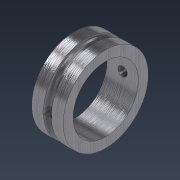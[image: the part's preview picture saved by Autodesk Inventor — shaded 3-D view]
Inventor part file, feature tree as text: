
AUTODESK INVENTOR PART (.ipt)
format: ipt  version: 2022 (Build 260153000, 153)  size: 160,256 bytes
history: native  units: mm
features: sketch x2, revolve x1, extrude x1
ambient origin geometry x8: Origin, YZ Plane, XZ Plane, XY Plane, X Axis, Y Axis, Z Axis, Center Point
bodies: Solid1 (feature_tree)
feature tree (4):
  revolve  "Revolution1"  [1 undecoded]
  extrude  "Extrusion1"  Depth=3.0mm
  sketch  "Sketch1"  dims[d0=200.0mm d1=65.0mm]
  sketch  "Sketch2"  dims[d2=24.0mm d3=3.0mm d4=90.0deg d5=50.0mm d6=7.0mm d7=0.0mm d8=0.0mm]
note: 1 required parameter value undecoded (feature->parameter linkage not recoverable at this tier; creation-order binding heuristic only, values carry confidence <= 0.55)
